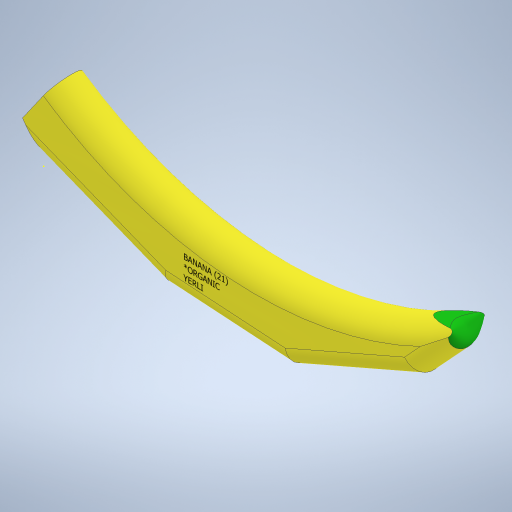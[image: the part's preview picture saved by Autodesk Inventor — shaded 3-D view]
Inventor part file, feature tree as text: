
AUTODESK INVENTOR PART (.ipt)
format: ipt  version: 2023.2 (Build 272271000, 271)  size: 334,336 bytes
history: native  units: mm
features: other x7, sketch x2, extrude x1
ambient origin geometry x8: Origin, YZ Plane, XZ Plane, XY Plane, X Axis, Y Axis, Z Axis, Center Point
bodies: Solid1 (feature_tree)
feature tree (10):
  extrude  "Extrusion1"  Depth=70.0mm
  other  "Full Round Fillet1"
  other  "Full Round Fillet2"
  other  "Full Round Fillet3"
  other  "Full Round Fillet4"
  other  "Full Round Fillet5"
  other  "Full Round Fillet6"
  other  "Full Round Fillet7"
  sketch  "Sketch2"  dims[d2=70.0mm d3=20.0mm d4=0.0mm]
  sketch  "Sketch1"  dims[d0=70.0mm d1=70.0mm]
